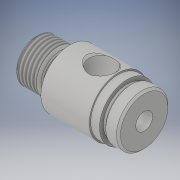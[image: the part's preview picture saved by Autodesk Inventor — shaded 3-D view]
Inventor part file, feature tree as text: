
AUTODESK INVENTOR PART (.ipt)
format: ipt  version: 2019 (Build 230136000, 136)  size: 251,392 bytes
history: native  units: mm
features: other x91, sketch x6, revolve x5, thread x1, extrude x1
ambient origin geometry x8: Origin, YZ Plane, XZ Plane, XY Plane, X Axis, Y Axis, Z Axis, Center Point
bodies: Solid1 (feature_tree)
feature tree (104):
  revolve  "Revolution1"  Angle=360.0deg
  revolve  "Revolution2"  Angle=360.0deg
  thread  "Thread1"  [1 undecoded]
  revolve  "Revolution3"  Angle=360.0deg
  extrude  "Extrusion1"  [1 undecoded]
  revolve  "Revolution4"  [1 undecoded]
  revolve  "Revolution5"  [1 undecoded]
  other  "b1_XY"
  other  "b1_YZ"
  other  "b1_ZX"
  other  "b1_X"
  other  "b1_Y"
  other  "b1_Z"
  other  "b1_Center"
  other  "b2_XY"
  other  "b2_YZ"
  other  "b2_ZX"
  other  "b2_X"
  other  "b2_Y"
  other  "b2_Z"
  other  "b2_Center"
  other  "cl1_XY"
  other  "cl1_YZ"
  other  "cl1_ZX"
  other  "cl1_X"
  other  "cl1_Y"
  other  "cl1_Z"
  other  "cl1_Center"
  other  "cl2_XY"
  other  "cl2_YZ"
  other  "cl2_ZX"
  other  "cl2_X"
  other  "cl2_Y"
  other  "cl2_Z"
  other  "cl2_Center"
  other  "ee_XY"
  other  "ee_YZ"
  other  "ee_ZX"
  other  "ee_X"
  other  "ee_Y"
  other  "ee_Z"
  other  "ee_Center"
  other  "od1_XY"
  other  "od1_YZ"
  other  "od1_ZX"
  other  "od1_X"
  other  "od1_Y"
  other  "od1_Z"
  other  "od1_Center"
  other  "od2_XY"
  other  "od2_YZ"
  other  "od2_ZX"
  other  "od2_X"
  other  "od2_Y"
  other  "od2_Z"
  other  "od2_Center"
  other  "od3_XY"
  other  "od3_YZ"
  other  "od3_ZX"
  other  "od3_X"
  other  "od3_Y"
  other  "od3_Z"
  other  "od3_Center"
  other  "od4_XY"
  other  "od4_YZ"
  other  "od4_ZX"
  other  "od4_X"
  other  "od4_Y"
  other  "od4_Z"
  other  "od4_Center"
  other  "to_body_XY"
  other  "to_body_YZ"
  other  "to_body_ZX"
  other  "to_body_X"
  other  "to_body_Y"
  other  "to_body_Z"
  other  "to_body_Center"
  other  "to_dummy_XY"
  other  "to_dummy_YZ"
  other  "to_dummy_ZX"
  other  "to_dummy_X"
  other  "to_dummy_Y"
  other  "to_dummy_Z"
  other  "to_dummy_Center"
  other  "to_nut_XY"
  other  "to_nut_YZ"
  other  "to_nut_ZX"
  other  "to_nut_X"
  other  "to_nut_Y"
  other  "to_nut_Z"
  other  "to_nut_Center"
  other  "to_stroke_adjuster_XY"
  other  "to_stroke_adjuster_YZ"
  other  "to_stroke_adjuster_ZX"
  other  "to_stroke_adjuster_X"
  other  "to_stroke_adjuster_Y"
  other  "to_stroke_adjuster_Z"
  other  "to_stroke_adjuster_Center"
  sketch  "Sketch_1"  dims[d0=360.0deg d1=360.0deg]
  sketch  "Sketch_2"  dims[d2=7.28853mm d3=0.0mm d4=360.0deg d5=111.0488mm d6=0.0mm]
  sketch  "Sketch_6"  dims[d7=360.0deg d8=360.0deg]
  sketch  "Sketch_7"  dims[d9=0.0mm d10=0.0mm d11=0.0mm d12=0.0mm d13=0.0mm d14=0.0mm d15=0.0mm d16=0.0mm d17=0.0mm d18=0.0mm]
  sketch  "Sketch_8"
  sketch  "Sketch_29"
note: 4 required parameter values undecoded (feature->parameter linkage not recoverable at this tier; creation-order binding heuristic only, values carry confidence <= 0.55)
